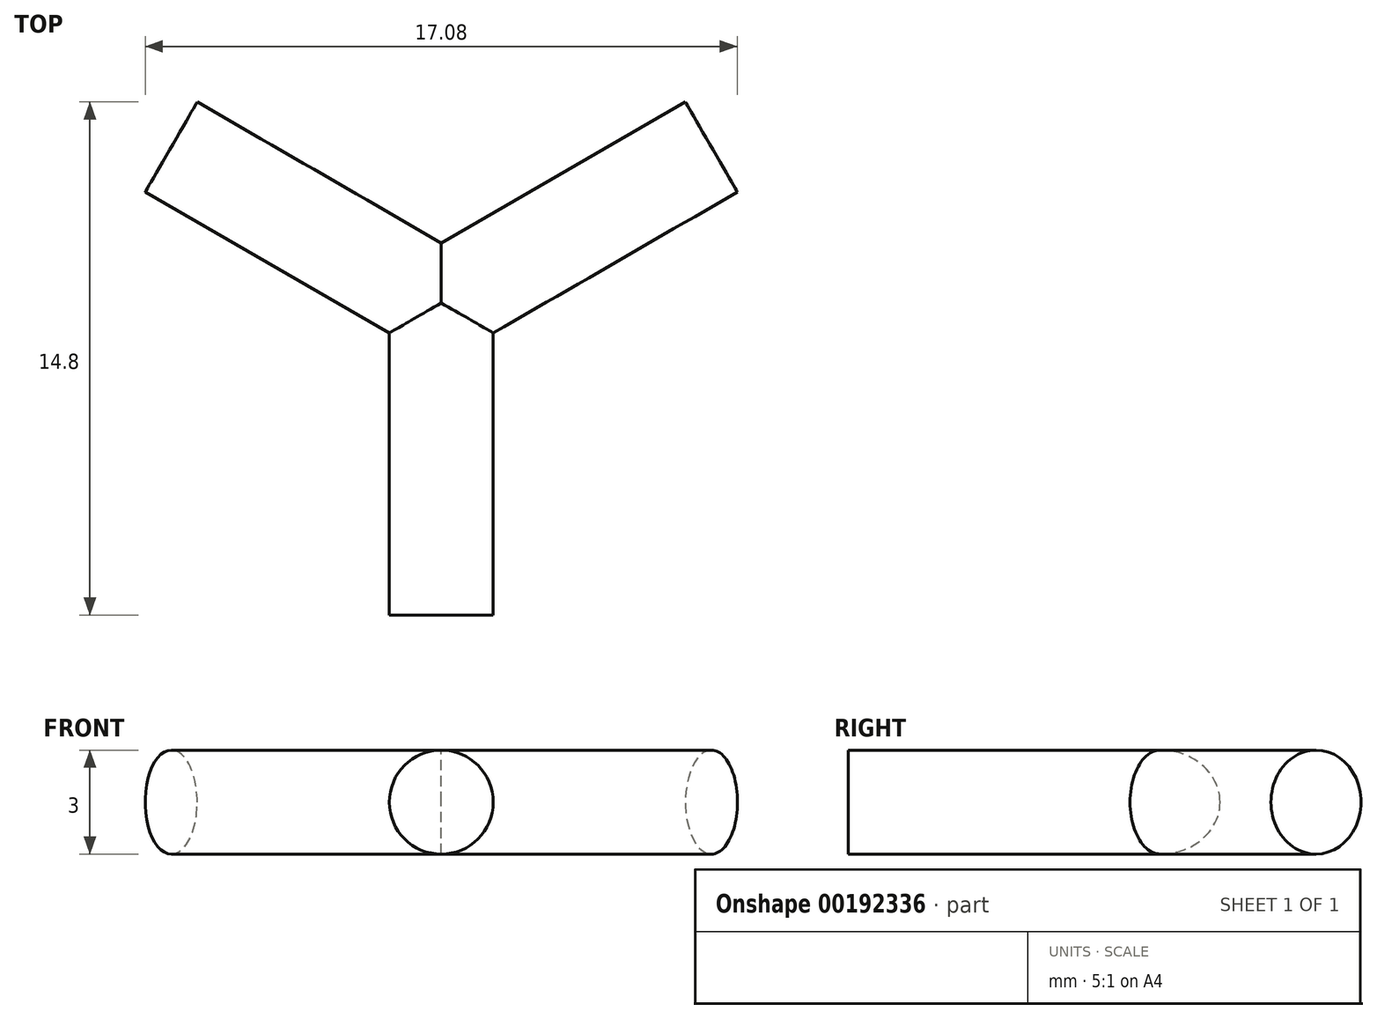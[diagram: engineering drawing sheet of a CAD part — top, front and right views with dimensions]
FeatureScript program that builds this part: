
annotation { "Feature Type Name" : "Feature", "Feature Type Description" : "" }
export const myFeature = defineFeature(function(context is Context, id is Id, definition is map)
    precondition{}
    {
        {
            var Q0;
            Q0=qCreatedBy(makeId("Top.planeOp"),FACE);
            var sketch = newSketch(context, id + "F0", { "sketchPlane" : qUnion([Q0])});
            skCircle(sketch, "E0.cCircle", {"center": v(0, 0) * mm, "radius": 9 * mm, "construction": true});
            skLineSegment(sketch, "E0.0", {"start": v(15.59, -9) * mm, "end": v(-15.59, -9) * mm, "construction": true});
            skLineSegment(sketch, "E0.1", {"start": v(-15.59, -9) * mm, "end": v(0, 18) * mm, "construction": true});
            skLineSegment(sketch, "E0.2", {"start": v(0, 18) * mm, "end": v(15.59, -9) * mm, "construction": true});
            skPoint(sketch, "E0.0.midPoint", {"position": v(0, -9) * mm});
            skLineSegment(sketch, "E1", {"start": v(0, 0) * mm, "end": v(-7.8, 4.5) * mm});
            skLineSegment(sketch, "E2", {"start": v(0, 0) * mm, "end": v(7.8, 4.5) * mm});
            skLineSegment(sketch, "E3", {"start": v(0, 0) * mm, "end": v(0, -9) * mm});
            skLineSegment(sketch, "E4", {"start": v(0, 0) * mm, "end": v(-0.75, -1.3) * mm});
            skLineSegment(sketch, "E5", {"start": v(-0.75, -1.3) * mm, "end": v(-8.54, 3.2) * mm});
            skLineSegment(sketch, "E6", {"start": v(-8.54, 3.2) * mm, "end": v(-7.8, 4.5) * mm});
            skLineSegment(sketch, "E7", {"start": v(0, 0) * mm, "end": v(-0.75, 1.3) * mm});
            skLineSegment(sketch, "E8", {"start": v(-0.75, 1.3) * mm, "end": v(7.04, 5.8) * mm});
            skLineSegment(sketch, "E9", {"start": v(7.04, 5.8) * mm, "end": v(7.8, 4.5) * mm});
            skLineSegment(sketch, "E10", {"start": v(0, 0) * mm, "end": v(1.5, 0) * mm});
            skLineSegment(sketch, "E11", {"start": v(1.5, 0) * mm, "end": v(1.5, -9) * mm});
            skLineSegment(sketch, "E12", {"start": v(1.5, -9) * mm, "end": v(0, -9) * mm});
            skSolve(sketch);
        }
        {
            var Q0;
            Q0=makeQuery(id+"F0.imprint","IMPRINT",FACE,{"disambiguationData":[TD([[makeQuery(id+"F0.imprint","IMPRINT",EDGE,{"derivedFrom":sQuery(id+"F0.wireOp",EDGE,"E1")}),1.0]])]});
            var Q1;
            Q1=sQuery(id+"F0.wireOp",EDGE,"E1");
            revolve(context, id + "F1", {"entities" : qUnion([Q0]), "axis" : qUnion([Q1]), "revolveType" : RevolveType.FULL});
        }
        {
            var Q0;
            Q0=makeQuery(id+"F0.imprint","IMPRINT",FACE,{"disambiguationData":[TD([[makeQuery(id+"F0.imprint","IMPRINT",EDGE,{"derivedFrom":sQuery(id+"F0.wireOp",EDGE,"E2")}),1.0]])]});
            var Q1;
            Q1=sQuery(id+"F0.wireOp",EDGE,"E2");
            revolve(context, id + "F2", {"operationType" : NewBodyOperationType.ADD, "entities" : qUnion([Q0]), "axis" : qUnion([Q1]), "revolveType" : RevolveType.FULL});
        }
        {
            var Q0;
            Q0=makeQuery(id+"F0.imprint","IMPRINT",FACE,{"disambiguationData":[TD([[makeQuery(id+"F0.imprint","IMPRINT",EDGE,{"derivedFrom":sQuery(id+"F0.wireOp",EDGE,"E3")}),1.0]])]});
            var Q1;
            Q1=sQuery(id+"F0.wireOp",EDGE,"E3");
            revolve(context, id + "F3", {"operationType" : NewBodyOperationType.ADD, "entities" : qUnion([Q0]), "axis" : qUnion([Q1]), "revolveType" : RevolveType.FULL});
        }
    });
